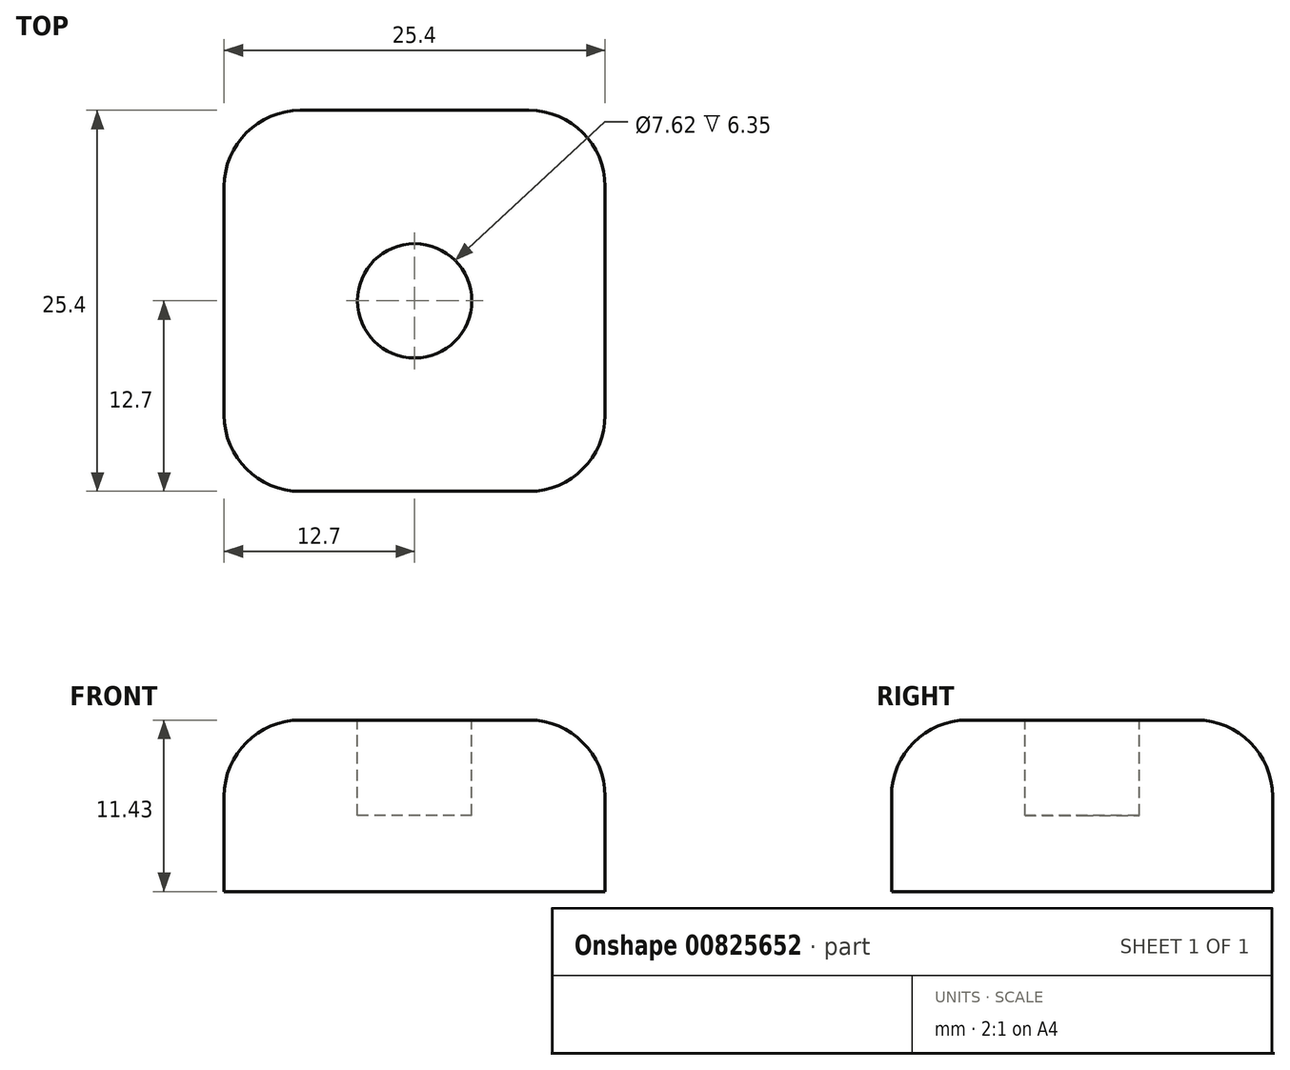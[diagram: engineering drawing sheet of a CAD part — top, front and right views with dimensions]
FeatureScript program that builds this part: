
annotation { "Feature Type Name" : "Feature", "Feature Type Description" : "" }
export const myFeature = defineFeature(function(context is Context, id is Id, definition is map)
    precondition{}
    {
        {
            var Q0;
            Q0=qCreatedBy(makeId("Top.planeOp"),FACE);
            var sketch = newSketch(context, id + "F0", { "sketchPlane" : qUnion([Q0])});
            skLineSegment(sketch, "E0", {"start": v(0, 0) * mm, "end": v(0, 25.4) * mm});
            skLineSegment(sketch, "E1", {"start": v(0, 25.4) * mm, "end": v(25.4, 25.4) * mm});
            skLineSegment(sketch, "E2", {"start": v(25.4, 25.4) * mm, "end": v(25.4, 0) * mm});
            skLineSegment(sketch, "E3", {"start": v(25.4, 0) * mm, "end": v(0, 0) * mm});
            skSolve(sketch);
        }
        {
            var Q0;
            Q0=makeQuery(id+"F0.imprint","IMPRINT",FACE,{"disambiguationData":[TD([[makeQuery(id+"F0.imprint","IMPRINT",EDGE,{"derivedFrom":sQuery(id+"F0.wireOp",EDGE,"E0")}),-1.0]])]});
            extrude(context, id + "F1", {"entities" : qUnion([Q0]), "depth" : 11.43 * mm, "offsetDistance" : 25.4 * mm});
        }
        {
            var Q0;
            Q0=makeQuery(id+"F1.opExtrude","CAP_FACE",FACE,{"disambiguationData":[OSD([sQuery(id+"F0.wireOp",EDGE,"E0"),sQuery(id+"F0.wireOp",EDGE,"E1"),sQuery(id+"F0.wireOp",EDGE,"E2"),sQuery(id+"F0.wireOp",EDGE,"E3")])],"isStart":false});
            var sketch = newSketch(context, id + "F2", { "sketchPlane" : qUnion([Q0])});
            skCircle(sketch, "E4", {"center": v(12.7, 12.7) * mm, "radius": 3.81 * mm});
            skSolve(sketch);
        }
        {
            var Q0;
            Q0 = qSketchRegion(id + "F2", true);
            extrude(context, id + "F3", {"entities" : qUnion([Q0]), "operationType" : NewBodyOperationType.REMOVE, "oppositeDirection" : true, "depth" : 6.35 * mm, "offsetDistance" : 25.4 * mm});
        }
        {
            var Q0;
            Q0=makeQuery(id+"F1.opExtrude","CAP_EDGE",EDGE,{"disambiguationData":[OSD([sQuery(id+"F0.wireOp",EDGE,"E2")])],"isStart":false});
            var Q1;
            Q1=makeQuery(id+"F1.opExtrude","CAP_EDGE",EDGE,{"disambiguationData":[OSD([sQuery(id+"F0.wireOp",EDGE,"E1")])],"isStart":false});
            var Q2;
            Q2=makeQuery(id+"F1.opExtrude","CAP_EDGE",EDGE,{"disambiguationData":[OSD([sQuery(id+"F0.wireOp",EDGE,"E0")])],"isStart":false});
            var Q3;
            Q3=makeQuery(id+"F1.opExtrude","CAP_EDGE",EDGE,{"disambiguationData":[OSD([sQuery(id+"F0.wireOp",EDGE,"E3")])],"isStart":false});
            var Q4;
            Q4=makeQuery(id+"F1.opExtrude","SWEPT_EDGE",EDGE,{"disambiguationData":[OSD([sQuery(id+"F0.wireOp",EDGE,"E1"),sQuery(id+"F0.wireOp",EDGE,"E2")])]});
            var Q5;
            Q5=makeQuery(id+"F1.opExtrude","SWEPT_EDGE",EDGE,{"disambiguationData":[OSD([sQuery(id+"F0.wireOp",EDGE,"E2"),sQuery(id+"F0.wireOp",EDGE,"E3")])]});
            var Q6;
            Q6=makeQuery(id+"F1.opExtrude","SWEPT_EDGE",EDGE,{"disambiguationData":[OSD([sQuery(id+"F0.wireOp",EDGE,"E0"),sQuery(id+"F0.wireOp",EDGE,"E1")])]});
            var Q7;
            Q7=makeQuery(id+"F1.opExtrude","SWEPT_EDGE",EDGE,{"disambiguationData":[OSD([sQuery(id+"F0.wireOp",EDGE,"E0"),sQuery(id+"F0.wireOp",EDGE,"E3")])]});
            fillet(context, id + "F4", {"entities" : qUnion([Q0, Q1, Q2, Q3, Q4, Q5, Q6, Q7]), "radius" : 5.08 * mm, "tangentPropagation" : true, "allowEdgeOverflow" : false});
        }
    });
